# Revit family: 30HS010X _BIM-Open-and-Closed
name_source: partatom
category: Specialty Equipment
units: mm (PartAtom-declared; Revit-internal decimal feet)

## family parameters
Cut with Voids When Loaded = No
Enable Cutting in Views = No
Host = Face
Maintain Annotation Orientation = No
Part Type = Normal
Room Calculation Point = No
Round Connector Dimension = Use Diameter
Shared = No

## types (2) — shared parameters
Assembly Code = E1090900
Default Elevation = 48 "
Description = Baby Changing Station as Specified
Keynote = 10812
Manufacturer = The Sova Company
Manufacturer Website = https://choosesova.com
Material(s) = High Density Polyethylene (HDPE) and Stainless Steel
Model = As Specified
Product Weight = 52.4lb
Recess Mounted = No
Revision = R1_4_2013
Surface Mounted = Yes
URL = https://choosesova.com
Unit Height = 21.9 "
Unit Length = 38.1 "
Weight Capacity = 250lb
zero-valued in all types: Expected Lifespan (Years), Maintenance Schedule (Months), Unit Weight, Warranty Duration (Years)

## per-type parameters (varying)
| type | Unit Depth |
| Closed | 5 " |
| Open | 17.2 " |

## geometry (parser evidence)
native form markers: Blend x10, Sweep x2
no freeform markers — native parametric forms only
